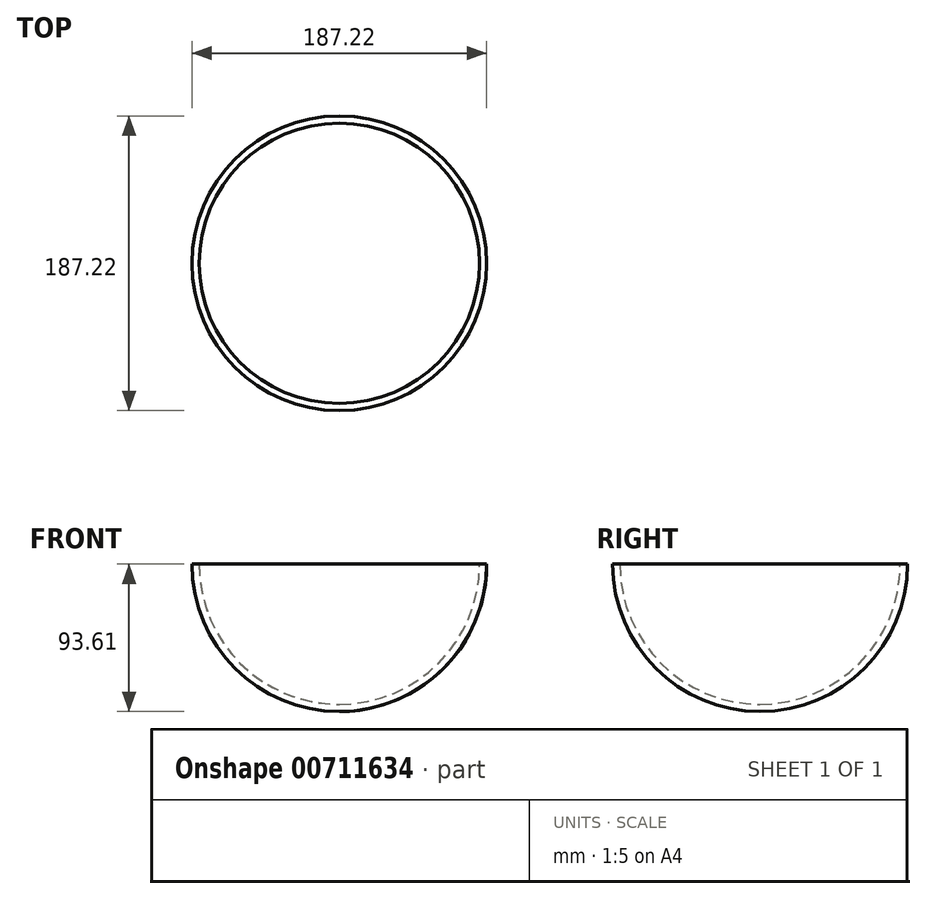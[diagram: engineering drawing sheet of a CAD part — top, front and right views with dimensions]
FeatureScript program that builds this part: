
annotation { "Feature Type Name" : "Feature", "Feature Type Description" : "" }
export const myFeature = defineFeature(function(context is Context, id is Id, definition is map)
    precondition{}
    {
        {
            var Q0;
            Q0=qCreatedBy(makeId("Front.planeOp"),FACE);
            var sketch = newSketch(context, id + "F0", { "sketchPlane" : qUnion([Q0])});
            skArc(sketch, "E0", {"start": v(93.6, 0) * mm, "mid": v(66.2, -66.2) * mm, "end": v(0, -93.6) * mm});
            skLineSegment(sketch, "E1", {"start": v(0, 0) * mm, "end": v(0, -93.6) * mm});
            skLineSegment(sketch, "E2", {"start": v(93.6, 0) * mm, "end": v(0, 0) * mm});
            skSolve(sketch);
        }
        {
            var Q0;
            Q0 = qSketchRegion(id + "F0", true);
            var Q1;
            Q1=sQuery(id+"F0.wireOp",EDGE,"E1");
            revolve(context, id + "F1", {"surfaceOperationType" : NewSurfaceOperationType.ADD, "entities" : qUnion([Q0]), "axis" : qUnion([Q1]), "revolveType" : RevolveType.FULL});
        }
        {
            var Q0;
            Q0=qCreatedBy(makeId("Front.planeOp"),FACE);
            var sketch = newSketch(context, id + "F2", { "sketchPlane" : qUnion([Q0])});
            skArc(sketch, "E3", {"start": v(0, -89.03) * mm, "mid": v(62.95, -62.95) * mm, "end": v(89.03, 0) * mm});
            skLineSegment(sketch, "E4", {"start": v(0, 0) * mm, "end": v(0, -89.03) * mm});
            skLineSegment(sketch, "E5", {"start": v(89.03, 0) * mm, "end": v(0, 0) * mm});
            skSolve(sketch);
        }
        {
            var Q0;
            Q0 = qSketchRegion(id + "F2", true);
            var Q1;
            Q1=sQuery(id+"F2.wireOp",EDGE,"E4");
            revolve(context, id + "F3", {"operationType" : NewBodyOperationType.REMOVE, "surfaceOperationType" : NewSurfaceOperationType.NEW, "entities" : qUnion([Q0]), "axis" : qUnion([Q1]), "revolveType" : RevolveType.FULL, "oppositeDirection" : true});
        }
    });
